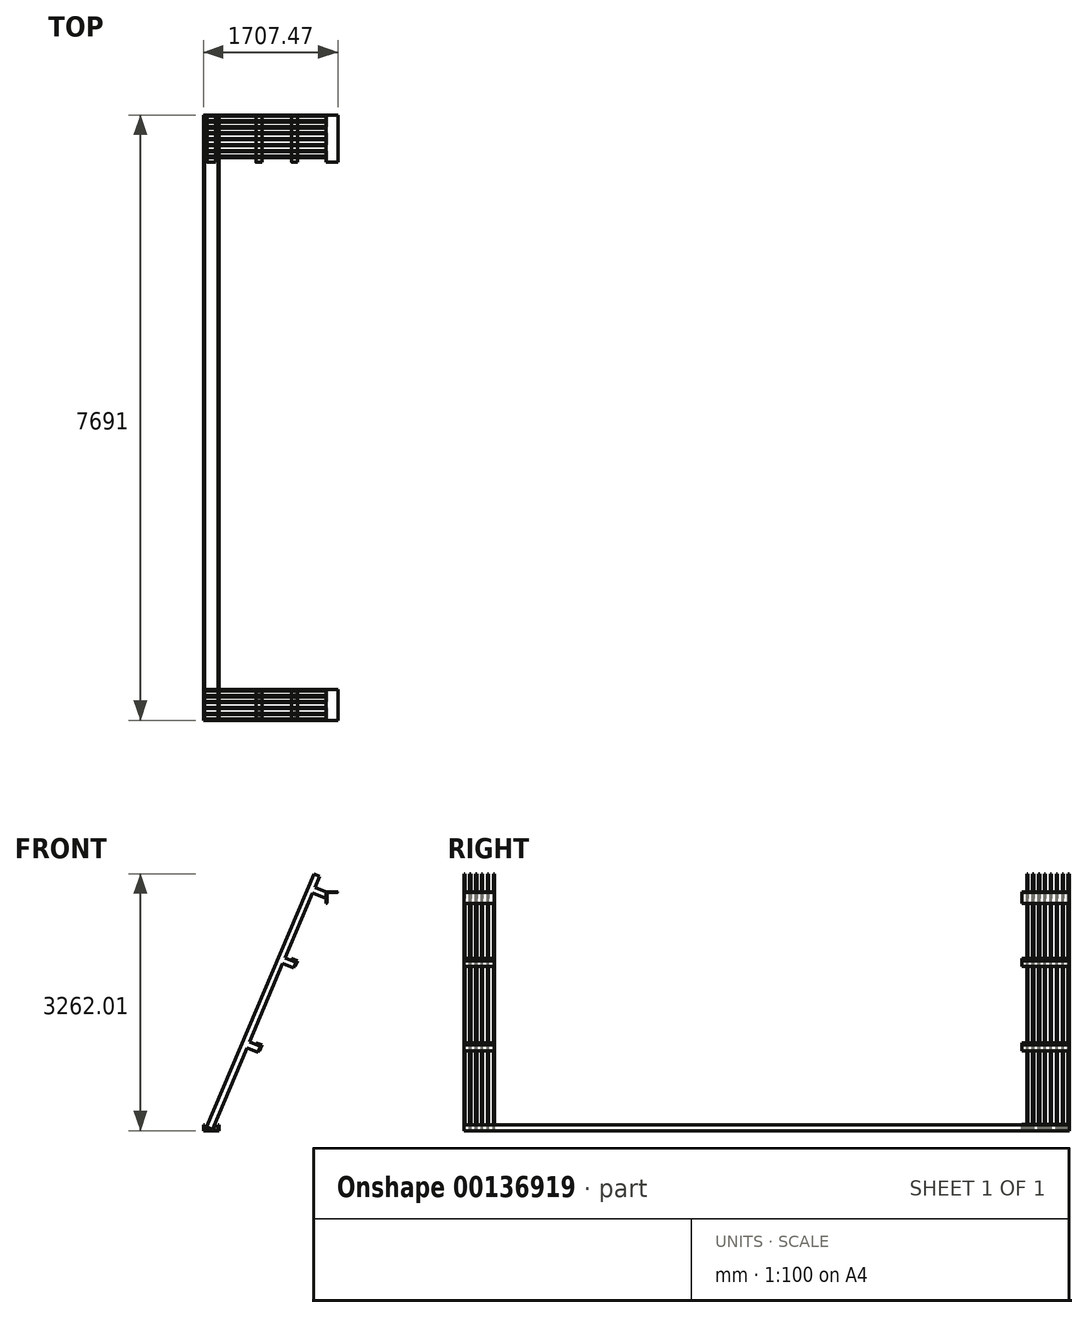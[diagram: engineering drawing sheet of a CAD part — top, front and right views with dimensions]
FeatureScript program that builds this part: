
annotation { "Feature Type Name" : "Feature", "Feature Type Description" : "" }
export const myFeature = defineFeature(function(context is Context, id is Id, definition is map)
    precondition{}
    {
        {
            var Q0;
            Q0=qCreatedBy(makeId("Front.planeOp"),FACE);
            var sketch = newSketch(context, id + "F0", { "sketchPlane" : qUnion([Q0])});
            skLineSegment(sketch, "E0", {"start": v(0, 0) * mm, "end": v(-200, 0) * mm});
            skLineSegment(sketch, "E1", {"start": v(-200, 0) * mm, "end": v(-200, 75) * mm});
            skLineSegment(sketch, "E2", {"start": v(0, 0) * mm, "end": v(0, 75) * mm});
            skLineSegment(sketch, "E3.0", {"start": v(-187.5, 18) * mm, "end": v(-187.5, 75) * mm});
            skLineSegment(sketch, "E4.0", {"start": v(-24.5, 6) * mm, "end": v(-175.5, 6) * mm});
            skLineSegment(sketch, "E5.0", {"start": v(-12.5, 18) * mm, "end": v(-12.5, 75) * mm});
            skLineSegment(sketch, "E6", {"start": v(-200, 75) * mm, "end": v(-187.5, 75) * mm});
            skLineSegment(sketch, "E7", {"start": v(-12.5, 75) * mm, "end": v(0, 75) * mm});
            skArc(sketch, "E8.filletArc", {"start": v(-187.5, 18) * mm, "mid": v(-183.99, 9.51) * mm, "end": v(-175.5, 6) * mm});
            skArc(sketch, "E9.filletArc", {"start": v(-24.5, 6) * mm, "mid": v(-16.01, 9.51) * mm, "end": v(-12.5, 18) * mm});
            skSolve(sketch);
        }
        {
            var Q0;
            Q0 = qSketchRegion(id + "F0", true);
            extrude(context, id + "F1", {"entities" : qUnion([Q0]), "depth" : 7151 * mm, "hasSecondDirection" : true, "secondDirectionOppositeDirection" : true, "secondDirectionDepth" : 540 * mm});
        }
        {
            var Q0;
            Q0=qCreatedBy(makeId("Front.planeOp"),FACE);
            var sketch = newSketch(context, id + "F2", { "sketchPlane" : qUnion([Q0])});
            skLineSegment(sketch, "E10", {"start": v(-80, 6) * mm, "end": v(-48.74, 79.64) * mm});
            skLineSegment(sketch, "E11", {"start": v(-80, 6) * mm, "end": v(-153.64, 37.26) * mm});
            skLineSegment(sketch, "E12", {"start": v(-153.64, 37.26) * mm, "end": v(-151.69, 41.86) * mm});
            skLineSegment(sketch, "E13", {"start": v(-145.13, 44.5) * mm, "end": v(-94.5, 23.02) * mm});
            skLineSegment(sketch, "E14", {"start": v(-81.4, 28.32) * mm, "end": v(-59.9, 78.95) * mm});
            skLineSegment(sketch, "E15", {"start": v(-53.34, 81.6) * mm, "end": v(-48.74, 79.64) * mm});
            skLineSegment(sketch, "E16", {"start": v(0, 0) * mm, "end": v(-293.4, 0) * mm, "construction": true});
            skPoint(sketch, "E17.visualSharp", {"position": v(-85.3, 19.11) * mm});
            skArc(sketch, "E17.filletArc", {"start": v(-94.5, 23.02) * mm, "mid": v(-86.85, 22.95) * mm, "end": v(-81.4, 28.32) * mm});
            skPoint(sketch, "E18.visualSharp", {"position": v(-57.95, 83.55) * mm});
            skArc(sketch, "E18.filletArc", {"start": v(-53.34, 81.6) * mm, "mid": v(-57.17, 81.63) * mm, "end": v(-59.9, 78.95) * mm});
            skPoint(sketch, "E19.visualSharp", {"position": v(-149.73, 46.46) * mm});
            skArc(sketch, "E19.filletArc", {"start": v(-145.13, 44.5) * mm, "mid": v(-148.96, 44.54) * mm, "end": v(-151.69, 41.86) * mm});
            skSolve(sketch);
        }
        {
            var Q0;
            Q0 = qSketchRegion(id + "F2", true);
            extrude(context, id + "F3", {"entities" : qUnion([Q0]), "oppositeDirection" : true, "depth" : 540 * mm, "hasSecondDirection" : true, "secondDirectionOppositeDirection" : false, "secondDirectionDepth" : 60 * mm});
        }
        {
            var Q0;
            Q0=qCreatedBy(makeId("Front.planeOp"),FACE);
            var sketch = newSketch(context, id + "F4", { "sketchPlane" : qUnion([Q0])});
            skLineSegment(sketch, "E20", {"start": v(541.8, 1086.98) * mm, "end": v(468.16, 1118.23) * mm});
            skLineSegment(sketch, "E21", {"start": v(541.8, 1086.98) * mm, "end": v(510.54, 1013.33) * mm});
            skLineSegment(sketch, "E22", {"start": v(510.54, 1013.33) * mm, "end": v(505.94, 1015.29) * mm});
            skLineSegment(sketch, "E23", {"start": v(503.3, 1021.84) * mm, "end": v(524.78, 1072.47) * mm});
            skLineSegment(sketch, "E24", {"start": v(519.48, 1085.58) * mm, "end": v(468.86, 1107.08) * mm});
            skLineSegment(sketch, "E25", {"start": v(466.2, 1113.63) * mm, "end": v(468.16, 1118.23) * mm});
            skLineSegment(sketch, "E26", {"start": v(210.54, 412.76) * mm, "end": v(-82.86, 412.76) * mm, "construction": true});
            skPoint(sketch, "E27.visualSharp", {"position": v(528.69, 1081.68) * mm});
            skArc(sketch, "E27.filletArc", {"start": v(524.78, 1072.47) * mm, "mid": v(524.85, 1080.13) * mm, "end": v(519.48, 1085.58) * mm});
            skPoint(sketch, "E28.visualSharp", {"position": v(464.25, 1109.03) * mm});
            skArc(sketch, "E28.filletArc", {"start": v(466.2, 1113.63) * mm, "mid": v(466.17, 1109.8) * mm, "end": v(468.86, 1107.08) * mm});
            skPoint(sketch, "E29.visualSharp", {"position": v(501.34, 1017.24) * mm});
            skArc(sketch, "E29.filletArc", {"start": v(503.3, 1021.84) * mm, "mid": v(503.26, 1018.02) * mm, "end": v(505.94, 1015.29) * mm});
            skLineSegment(sketch, "E30", {"start": v(0, 0) * mm, "end": v(-82.56, 0) * mm, "construction": true});
            skLineSegment(sketch, "E31", {"start": v(0, 0) * mm, "end": v(0, 124.95) * mm, "construction": true});
            skLineSegment(sketch, "E32", {"start": v(0, 0) * mm, "end": v(302.9, 0) * mm, "construction": true});
            skLineSegment(sketch, "E33.0", {"start": v(0, 6) * mm, "end": v(302.9, 6) * mm, "construction": true});
            skLineSegment(sketch, "E34", {"start": v(0, 6) * mm, "end": v(-80, 6) * mm, "construction": true});
            skLineSegment(sketch, "E35", {"start": v(-80, 6) * mm, "end": v(1212.93, 3051.95) * mm, "construction": true});
            skLineSegment(sketch, "E36.0", {"start": v(-89.2, 9.9) * mm, "end": v(353.5, 1052.84) * mm});
            skLineSegment(sketch, "E37", {"start": v(-80, 6) * mm, "end": v(-174.08, 45.94) * mm, "construction": true});
            skLineSegment(sketch, "E38.0", {"start": v(-76.1, 15.2) * mm, "end": v(-170.18, 55.14) * mm});
            skLineSegment(sketch, "E39.0", {"start": v(507.2, 1031.05) * mm, "end": v(284.24, 1125.69) * mm, "construction": true});
            skLineSegment(sketch, "E40.0", {"start": v(961.62, 2101.6) * mm, "end": v(738.67, 2196.24) * mm, "construction": true});
            skLineSegment(sketch, "E41.0", {"start": v(1341.8, 2997.25) * mm, "end": v(1118.85, 3091.89) * mm});
            skLineSegment(sketch, "E42.0", {"start": v(48.87, -48.7) * mm, "end": v(72.1, 6) * mm});
            skLineSegment(sketch, "E43.0", {"start": v(522.83, 1067.87) * mm, "end": v(384.75, 1126.48) * mm});
            skLineSegment(sketch, "E44.0", {"start": v(491.57, 994.23) * mm, "end": v(353.5, 1052.84) * mm});
            skLineSegment(sketch, "E45.0", {"start": v(977.25, 2138.42) * mm, "end": v(839.17, 2197.03) * mm});
            skLineSegment(sketch, "E46.0", {"start": v(945.99, 2064.78) * mm, "end": v(807.91, 2123.39) * mm});
            skLineSegment(sketch, "E47.0", {"start": v(-162.85, 41.17) * mm, "end": v(1204.32, 3262.01) * mm});
            skLineSegment(sketch, "E48.trimOffspring", {"start": v(384.75, 1126.48) * mm, "end": v(807.91, 2123.39) * mm});
            skLineSegment(sketch, "E49.trimOffspring", {"start": v(945.99, 2064.78) * mm, "end": v(977.25, 2138.42) * mm});
            skLineSegment(sketch, "E50.trimOffspring", {"start": v(491.57, 994.23) * mm, "end": v(522.83, 1067.87) * mm});
            skLineSegment(sketch, "E51.0", {"start": v(1277.96, 3230.75) * mm, "end": v(1204.32, 3262.01) * mm});
            skLineSegment(sketch, "E52.0", {"start": v(1357.43, 3034.07) * mm, "end": v(1219.35, 3092.68) * mm});
            skLineSegment(sketch, "E53.0", {"start": v(1357.43, 2947.16) * mm, "end": v(1188.1, 3019.04) * mm});
            skLineSegment(sketch, "E54.trimOffspring", {"start": v(839.17, 2197.03) * mm, "end": v(1277.96, 3230.75) * mm});
            skLineSegment(sketch, "E55", {"start": v(1357.43, 3034.07) * mm, "end": v(1357.43, 2947.16) * mm});
            skLineSegment(sketch, "E56", {"start": v(1357.43, 3034.07) * mm, "end": v(1507.43, 3034.07) * mm});
            skLineSegment(sketch, "E57", {"start": v(1357.43, 3034.07) * mm, "end": v(1357.43, 2884.07) * mm});
            skLineSegment(sketch, "E58.0", {"start": v(1383.43, 3024.07) * mm, "end": v(1499.47, 3024.07) * mm});
            skLineSegment(sketch, "E59.0", {"start": v(1367.43, 3008.07) * mm, "end": v(1367.43, 2892.07) * mm});
            skLineSegment(sketch, "E60", {"start": v(1357.43, 2884.07) * mm, "end": v(1359.43, 2884.07) * mm});
            skLineSegment(sketch, "E61", {"start": v(1507.43, 3034.07) * mm, "end": v(1507.47, 3032.25) * mm});
            skArc(sketch, "E62.filletArc", {"start": v(1383.43, 3024.07) * mm, "mid": v(1372.12, 3019.38) * mm, "end": v(1367.43, 3008.07) * mm});
            skPoint(sketch, "E63.visualSharp", {"position": v(1507.65, 3024.07) * mm});
            skArc(sketch, "E63.filletArc", {"start": v(1499.47, 3024.07) * mm, "mid": v(1505.2, 3026.47) * mm, "end": v(1507.47, 3032.25) * mm});
            skPoint(sketch, "E64.visualSharp", {"position": v(1367.43, 2884.07) * mm});
            skArc(sketch, "E64.filletArc", {"start": v(1359.43, 2884.07) * mm, "mid": v(1365.09, 2886.41) * mm, "end": v(1367.43, 2892.07) * mm});
            skLineSegment(sketch, "E65.0", {"start": v(541.8, 1086.98) * mm, "end": v(394.52, 1149.5) * mm, "construction": true});
            skLineSegment(sketch, "E66.0", {"start": v(500.77, 990.32) * mm, "end": v(541.8, 1086.98) * mm, "construction": true});
            skLineSegment(sketch, "E67", {"start": v(996.22, 2157.52) * mm, "end": v(922.58, 2188.78) * mm});
            skLineSegment(sketch, "E68", {"start": v(996.22, 2157.52) * mm, "end": v(964.96, 2083.88) * mm});
            skLineSegment(sketch, "E69", {"start": v(964.96, 2083.88) * mm, "end": v(960.36, 2085.84) * mm});
            skLineSegment(sketch, "E70", {"start": v(957.71, 2092.4) * mm, "end": v(979.2, 2143.02) * mm});
            skLineSegment(sketch, "E71", {"start": v(973.9, 2156.13) * mm, "end": v(923.28, 2177.62) * mm});
            skLineSegment(sketch, "E72", {"start": v(920.63, 2184.18) * mm, "end": v(922.58, 2188.78) * mm});
            skPoint(sketch, "E73.visualSharp", {"position": v(983.1, 2152.22) * mm});
            skArc(sketch, "E73.filletArc", {"start": v(979.2, 2143.02) * mm, "mid": v(979.27, 2150.67) * mm, "end": v(973.9, 2156.13) * mm});
            skArc(sketch, "E74.filletArc", {"start": v(920.63, 2184.18) * mm, "mid": v(920.6, 2180.35) * mm, "end": v(923.28, 2177.62) * mm});
            skPoint(sketch, "E75.visualSharp", {"position": v(955.76, 2087.79) * mm});
            skArc(sketch, "E75.filletArc", {"start": v(957.71, 2092.4) * mm, "mid": v(957.68, 2088.57) * mm, "end": v(960.36, 2085.84) * mm});
            skLineSegment(sketch, "E76.0", {"start": v(955.2, 2060.87) * mm, "end": v(996.22, 2157.52) * mm});
            skLineSegment(sketch, "E77.trimOffspring", {"start": v(858.15, 2216.13) * mm, "end": v(848.94, 2220.04) * mm});
            skSolve(sketch);
        }
        {
            var Q0;
            Q0=makeQuery(id+"F4.imprint","IMPRINT",FACE,{"disambiguationData":[TD([[makeQuery(id+"F4.imprint","IMPRINT",EDGE,{"derivedFrom":sQuery(id+"F4.wireOp",EDGE,"E20")}),1.0]])]});
            var Q1;
            {var subQ1=sQuery(id+"F4.wireOp",EDGE,"E56");Q1=makeQuery(id+"F4.imprint","IMPRINT",FACE,{"disambiguationData":[TD([[makeQuery(id+"F4.imprint","IMPRINT",EDGE,{"derivedFrom":subQ1}),-1.0]])]});}
            var Q2;
            {var subQ1=sQuery(id+"F4.wireOp",EDGE,"E69");Q2=makeQuery(id+"F4.imprint","IMPRINT",FACE,{"disambiguationData":[TD([[makeQuery(id+"F4.imprint","IMPRINT",EDGE,{"derivedFrom":subQ1}),-1.0]])]});}
            var Q3;
            {var subQ1=sQuery(id+"F4.wireOp",EDGE,"E69");Q3=makeQuery(id+"F4.imprint","IMPRINT",FACE,{"disambiguationData":[TD([[makeQuery(id+"F4.imprint","IMPRINT",EDGE,{"derivedFrom":subQ1}),-1.0]])]});}
            extrude(context, id + "F5", {"entities" : qUnion([Q0, Q1, Q2, Q3]), "oppositeDirection" : true, "depth" : 540 * mm, "hasSecondDirection" : true, "secondDirectionOppositeDirection" : false, "secondDirectionDepth" : 60 * mm});
        }
        {
            var Q0;
            {var subQ4=sQuery(id+"F4.wireOp",EDGE,"E51.0");Q0=makeQuery(id+"F4.imprint","IMPRINT",FACE,{"disambiguationData":[TD([[makeQuery(id+"F4.imprint","IMPRINT",EDGE,{"derivedFrom":subQ4}),1.0]])]});}
            var Q1;
            {var subQ10=sQuery(id+"F4.wireOp",EDGE,"E43.0");Q1=makeQuery(id+"F4.imprint","IMPRINT",FACE,{"disambiguationData":[TD([[makeQuery(id+"F4.imprint","IMPRINT",EDGE,{"derivedFrom":subQ10}),1.0]])]});}
            var Q2;
            {var subQ1=sQuery(id+"F4.wireOp",EDGE,"E52.0");Q2=makeQuery(id+"F4.imprint","IMPRINT",FACE,{"disambiguationData":[TD([[makeQuery(id+"F4.imprint","IMPRINT",EDGE,{"derivedFrom":subQ1}),1.0]])]});}
            extrude(context, id + "F6", {"entities" : qUnion([Q0, Q1, Q2]), "oppositeDirection" : true, "depth" : 15 * mm});
        }
        {
            var Q0;
            Q0=qCreatedBy(makeId("Front.planeOp"),FACE);
            cPlane(context, id + "F7", {"entities" : qUnion([Q0]), "cplaneType" : CPlaneType.OFFSET, "offset" : 90 * mm, "oppositeDirection" : true, "width" : 150 * mm, "height" : 150 * mm});
        }
        {
            var Q0;
            Q0=qCreatedBy(id+"F7.planeOp",FACE);
            var sketch = newSketch(context, id + "F8", { "sketchPlane" : qUnion([Q0])});
            skLineSegment(sketch, "E78", {"start": v(541.8, 1086.98) * mm, "end": v(468.16, 1118.23) * mm});
            skLineSegment(sketch, "E79", {"start": v(541.8, 1086.98) * mm, "end": v(510.54, 1013.33) * mm});
            skLineSegment(sketch, "E80", {"start": v(510.54, 1013.33) * mm, "end": v(505.94, 1015.29) * mm});
            skLineSegment(sketch, "E81", {"start": v(503.3, 1021.84) * mm, "end": v(524.78, 1072.47) * mm});
            skLineSegment(sketch, "E82", {"start": v(519.48, 1085.58) * mm, "end": v(468.86, 1107.08) * mm});
            skLineSegment(sketch, "E83", {"start": v(466.2, 1113.63) * mm, "end": v(468.16, 1118.23) * mm});
            skLineSegment(sketch, "E84", {"start": v(1436.56, -795.55) * mm, "end": v(1143.16, -795.55) * mm, "construction": true});
            skPoint(sketch, "E85.visualSharp", {"position": v(528.69, 1081.68) * mm});
            skArc(sketch, "E85.filletArc", {"start": v(524.78, 1072.47) * mm, "mid": v(524.85, 1080.13) * mm, "end": v(519.48, 1085.58) * mm});
            skPoint(sketch, "E86.visualSharp", {"position": v(464.25, 1109.03) * mm});
            skArc(sketch, "E86.filletArc", {"start": v(466.2, 1113.63) * mm, "mid": v(466.17, 1109.8) * mm, "end": v(468.86, 1107.08) * mm});
            skPoint(sketch, "E87.visualSharp", {"position": v(501.34, 1017.24) * mm});
            skArc(sketch, "E87.filletArc", {"start": v(503.3, 1021.84) * mm, "mid": v(503.26, 1018.02) * mm, "end": v(505.94, 1015.29) * mm});
            skLineSegment(sketch, "E88", {"start": v(0, 0) * mm, "end": v(-82.56, 0) * mm, "construction": true});
            skLineSegment(sketch, "E89", {"start": v(0, 0) * mm, "end": v(0, 124.95) * mm, "construction": true});
            skLineSegment(sketch, "E90", {"start": v(0, 0) * mm, "end": v(302.9, 0) * mm, "construction": true});
            skLineSegment(sketch, "E91.0", {"start": v(0, 6) * mm, "end": v(302.9, 6) * mm, "construction": true});
            skLineSegment(sketch, "E92", {"start": v(0, 6) * mm, "end": v(-80, 6) * mm, "construction": true});
            skLineSegment(sketch, "E93", {"start": v(-80, 6) * mm, "end": v(1212.93, 3051.95) * mm, "construction": true});
            skLineSegment(sketch, "E94.0", {"start": v(-89.2, 9.9) * mm, "end": v(353.5, 1052.84) * mm});
            skLineSegment(sketch, "E95", {"start": v(-80, 6) * mm, "end": v(-174.08, 45.94) * mm, "construction": true});
            skLineSegment(sketch, "E96.0", {"start": v(-76.1, 15.2) * mm, "end": v(-170.18, 55.14) * mm});
            skLineSegment(sketch, "E97.0", {"start": v(507.2, 1031.05) * mm, "end": v(284.24, 1125.69) * mm, "construction": true});
            skLineSegment(sketch, "E98.0", {"start": v(961.62, 2101.6) * mm, "end": v(738.67, 2196.24) * mm, "construction": true});
            skLineSegment(sketch, "E99.0", {"start": v(1341.8, 2997.25) * mm, "end": v(1118.85, 3091.89) * mm});
            skLineSegment(sketch, "E100.0", {"start": v(48.87, -48.7) * mm, "end": v(72.1, 6) * mm});
            skLineSegment(sketch, "E101.0", {"start": v(522.83, 1067.87) * mm, "end": v(384.75, 1126.48) * mm});
            skLineSegment(sketch, "E102.0", {"start": v(491.57, 994.23) * mm, "end": v(353.5, 1052.84) * mm});
            skLineSegment(sketch, "E103.0", {"start": v(977.25, 2138.42) * mm, "end": v(839.17, 2197.03) * mm});
            skLineSegment(sketch, "E104.0", {"start": v(945.99, 2064.78) * mm, "end": v(807.91, 2123.39) * mm});
            skLineSegment(sketch, "E105.0", {"start": v(-162.85, 41.17) * mm, "end": v(1204.32, 3262.01) * mm});
            skLineSegment(sketch, "E106.trimOffspring", {"start": v(384.75, 1126.48) * mm, "end": v(807.91, 2123.39) * mm});
            skLineSegment(sketch, "E107.trimOffspring", {"start": v(945.99, 2064.78) * mm, "end": v(977.25, 2138.42) * mm});
            skLineSegment(sketch, "E108.trimOffspring", {"start": v(491.57, 994.23) * mm, "end": v(522.83, 1067.87) * mm});
            skLineSegment(sketch, "E109.0", {"start": v(1277.96, 3230.75) * mm, "end": v(1204.32, 3262.01) * mm});
            skLineSegment(sketch, "E110.0", {"start": v(1357.43, 3034.07) * mm, "end": v(1219.35, 3092.68) * mm});
            skLineSegment(sketch, "E111.0", {"start": v(1357.43, 2947.16) * mm, "end": v(1188.1, 3019.04) * mm});
            skLineSegment(sketch, "E112.trimOffspring", {"start": v(839.17, 2197.03) * mm, "end": v(1277.96, 3230.75) * mm});
            skLineSegment(sketch, "E113", {"start": v(1357.43, 3034.07) * mm, "end": v(1357.43, 2947.16) * mm});
            skLineSegment(sketch, "E114", {"start": v(1357.43, 3034.07) * mm, "end": v(1507.43, 3034.07) * mm});
            skLineSegment(sketch, "E115", {"start": v(1357.43, 3034.07) * mm, "end": v(1357.43, 2884.07) * mm});
            skLineSegment(sketch, "E116.0", {"start": v(1383.43, 3024.07) * mm, "end": v(1499.47, 3024.07) * mm});
            skLineSegment(sketch, "E117.0", {"start": v(1367.43, 3008.07) * mm, "end": v(1367.43, 2892.07) * mm});
            skLineSegment(sketch, "E118", {"start": v(1357.43, 2884.07) * mm, "end": v(1359.43, 2884.07) * mm});
            skLineSegment(sketch, "E119", {"start": v(1507.43, 3034.07) * mm, "end": v(1507.47, 3032.25) * mm});
            skArc(sketch, "E120.filletArc", {"start": v(1383.43, 3024.07) * mm, "mid": v(1372.12, 3019.38) * mm, "end": v(1367.43, 3008.07) * mm});
            skPoint(sketch, "E121.visualSharp", {"position": v(1507.65, 3024.07) * mm});
            skArc(sketch, "E121.filletArc", {"start": v(1499.47, 3024.07) * mm, "mid": v(1505.2, 3026.47) * mm, "end": v(1507.47, 3032.25) * mm});
            skPoint(sketch, "E122.visualSharp", {"position": v(1367.43, 2884.07) * mm});
            skArc(sketch, "E122.filletArc", {"start": v(1359.43, 2884.07) * mm, "mid": v(1365.09, 2886.41) * mm, "end": v(1367.43, 2892.07) * mm});
            skLineSegment(sketch, "E123.0", {"start": v(541.8, 1086.98) * mm, "end": v(394.52, 1149.5) * mm, "construction": true});
            skLineSegment(sketch, "E124.0", {"start": v(500.77, 990.32) * mm, "end": v(541.8, 1086.98) * mm, "construction": true});
            skLineSegment(sketch, "E125", {"start": v(996.22, 2157.52) * mm, "end": v(922.58, 2188.78) * mm});
            skLineSegment(sketch, "E126", {"start": v(996.22, 2157.52) * mm, "end": v(964.96, 2083.88) * mm});
            skLineSegment(sketch, "E127", {"start": v(964.96, 2083.88) * mm, "end": v(960.36, 2085.84) * mm});
            skLineSegment(sketch, "E128", {"start": v(957.71, 2092.4) * mm, "end": v(979.2, 2143.02) * mm});
            skLineSegment(sketch, "E129", {"start": v(973.9, 2156.13) * mm, "end": v(923.28, 2177.62) * mm});
            skLineSegment(sketch, "E130", {"start": v(920.63, 2184.18) * mm, "end": v(922.58, 2188.78) * mm});
            skPoint(sketch, "E131.visualSharp", {"position": v(983.1, 2152.22) * mm});
            skArc(sketch, "E131.filletArc", {"start": v(979.2, 2143.02) * mm, "mid": v(979.27, 2150.67) * mm, "end": v(973.9, 2156.13) * mm});
            skArc(sketch, "E132.filletArc", {"start": v(920.63, 2184.18) * mm, "mid": v(920.6, 2180.35) * mm, "end": v(923.28, 2177.62) * mm});
            skPoint(sketch, "E133.visualSharp", {"position": v(955.76, 2087.79) * mm});
            skArc(sketch, "E133.filletArc", {"start": v(957.71, 2092.4) * mm, "mid": v(957.68, 2088.57) * mm, "end": v(960.36, 2085.84) * mm});
            skLineSegment(sketch, "E134.0", {"start": v(955.2, 2060.87) * mm, "end": v(996.22, 2157.52) * mm});
            skLineSegment(sketch, "E135.trimOffspring", {"start": v(858.15, 2216.13) * mm, "end": v(848.94, 2220.04) * mm});
            skLineSegment(sketch, "E136", {"start": v(1219.35, 3092.68) * mm, "end": v(1250.61, 3166.32) * mm});
            skLineSegment(sketch, "E137", {"start": v(1250.61, 3166.32) * mm, "end": v(1324.25, 3135.06) * mm});
            skLineSegment(sketch, "E138", {"start": v(1324.25, 3135.06) * mm, "end": v(1293, 3061.42) * mm});
            skLineSegment(sketch, "E139", {"start": v(1293, 3061.42) * mm, "end": v(1219.35, 3092.68) * mm});
            skCircle(sketch, "E140", {"center": v(1271.8, 3113.87) * mm, "radius": 12.89 * mm});
            skSolve(sketch);
        }
        {
            var Q0;
            {var subQ16=sQuery(id+"F8.wireOp",EDGE,"E101.0");Q0=makeQuery(id+"F8.imprint","IMPRINT",FACE,{"disambiguationData":[TD([[makeQuery(id+"F8.imprint","IMPRINT",EDGE,{"derivedFrom":subQ16}),1.0]])]});}
            var Q1;
            {var subQ4=sQuery(id+"F8.wireOp",EDGE,"E110.0");Q1=makeQuery(id+"F8.imprint","IMPRINT",FACE,{"disambiguationData":[TD([[makeQuery(id+"F8.imprint","IMPRINT",EDGE,{"derivedFrom":subQ4}),1.0]])]});}
            var Q2;
            Q2=makeQuery(id+"F8.imprint","IMPRINT",FACE,{"disambiguationData":[TD([[makeQuery(id+"F8.imprint","IMPRINT",EDGE,{"derivedFrom":sQuery(id+"F8.wireOp",EDGE,"E136")}),-1.0]])]});
            var Q3;
            {var subQ4=sQuery(id+"F8.wireOp",EDGE,"E109.0");Q3=makeQuery(id+"F8.imprint","IMPRINT",FACE,{"disambiguationData":[TD([[makeQuery(id+"F8.imprint","IMPRINT",EDGE,{"derivedFrom":subQ4}),1.0]])]});}
            extrude(context, id + "F9", {"entities" : qUnion([Q0, Q1, Q2, Q3]), "depth" : 15 * mm});
        }
        {
            var Q0;
            Q0=makeQuery(id+"F6.opExtrude","SWEPT_BODY",BODY,{"disambiguationData":[OSD([sQuery(id+"F4.wireOp",EDGE,"E36.0"),sQuery(id+"F4.wireOp",EDGE,"E38.0"),sQuery(id+"F4.wireOp",EDGE,"E43.0"),sQuery(id+"F4.wireOp",EDGE,"E44.0"),sQuery(id+"F4.wireOp",EDGE,"E45.0"),sQuery(id+"F4.wireOp",EDGE,"E46.0"),sQuery(id+"F4.wireOp",EDGE,"E47.0"),sQuery(id+"F4.wireOp",EDGE,"E48.trimOffspring"),sQuery(id+"F4.wireOp",EDGE,"E49.trimOffspring"),sQuery(id+"F4.wireOp",EDGE,"E50.trimOffspring"),sQuery(id+"F4.wireOp",EDGE,"E51.0"),sQuery(id+"F4.wireOp",EDGE,"E52.0"),sQuery(id+"F4.wireOp",EDGE,"E53.0"),sQuery(id+"F4.wireOp",EDGE,"E54.trimOffspring"),sQuery(id+"F4.wireOp",EDGE,"E57"),sQuery(id+"F4.wireOp",EDGE,"E70")])]});
            var Q1;
            Q1=makeQuery(id+"F5.opExtrude","SWEPT_EDGE",EDGE,{"disambiguationData":[OSD([sQuery(id+"F4.wireOp",EDGE,"E52.0"),sQuery(id+"F4.wireOp",EDGE,"E56"),sQuery(id+"F4.wireOp",EDGE,"E57")])]});
            transform(context, id + "F10", {"entities" : qUnion([Q0]), "transformType" : TransformType.TRANSLATION_3D, "dx" : 0 * mm, "dy" : 150 * mm, "dz" : 0 * mm, "makeCopy" : true});
        }
        {
            var Q0;
            Q0=makeQuery(id+"F10.opPattern","COPY",BODY,{"derivedFrom":makeQuery(id+"F6.opExtrude","SWEPT_BODY",BODY,{"disambiguationData":[OSD([sQuery(id+"F4.wireOp",EDGE,"E36.0"),sQuery(id+"F4.wireOp",EDGE,"E38.0"),sQuery(id+"F4.wireOp",EDGE,"E43.0"),sQuery(id+"F4.wireOp",EDGE,"E44.0"),sQuery(id+"F4.wireOp",EDGE,"E45.0"),sQuery(id+"F4.wireOp",EDGE,"E46.0"),sQuery(id+"F4.wireOp",EDGE,"E47.0"),sQuery(id+"F4.wireOp",EDGE,"E48.trimOffspring"),sQuery(id+"F4.wireOp",EDGE,"E49.trimOffspring"),sQuery(id+"F4.wireOp",EDGE,"E50.trimOffspring"),sQuery(id+"F4.wireOp",EDGE,"E51.0"),sQuery(id+"F4.wireOp",EDGE,"E52.0"),sQuery(id+"F4.wireOp",EDGE,"E53.0"),sQuery(id+"F4.wireOp",EDGE,"E54.trimOffspring"),sQuery(id+"F4.wireOp",EDGE,"E57"),sQuery(id+"F4.wireOp",EDGE,"E70")])]}),"instanceName":"1"});
            transform(context, id + "F11", {"entities" : qUnion([Q0]), "transformType" : TransformType.TRANSLATION_3D, "dx" : 0 * mm, "dy" : 75 * mm, "dz" : 0 * mm, "makeCopy" : true});
        }
        {
            var Q0;
            Q0=makeQuery(id+"F11.opPattern","COPY",BODY,{"derivedFrom":makeQuery(id+"F10.opPattern","COPY",BODY,{"derivedFrom":makeQuery(id+"F6.opExtrude","SWEPT_BODY",BODY,{"disambiguationData":[OSD([sQuery(id+"F4.wireOp",EDGE,"E36.0"),sQuery(id+"F4.wireOp",EDGE,"E38.0"),sQuery(id+"F4.wireOp",EDGE,"E43.0"),sQuery(id+"F4.wireOp",EDGE,"E44.0"),sQuery(id+"F4.wireOp",EDGE,"E45.0"),sQuery(id+"F4.wireOp",EDGE,"E46.0"),sQuery(id+"F4.wireOp",EDGE,"E47.0"),sQuery(id+"F4.wireOp",EDGE,"E48.trimOffspring"),sQuery(id+"F4.wireOp",EDGE,"E49.trimOffspring"),sQuery(id+"F4.wireOp",EDGE,"E50.trimOffspring"),sQuery(id+"F4.wireOp",EDGE,"E51.0"),sQuery(id+"F4.wireOp",EDGE,"E52.0"),sQuery(id+"F4.wireOp",EDGE,"E53.0"),sQuery(id+"F4.wireOp",EDGE,"E54.trimOffspring"),sQuery(id+"F4.wireOp",EDGE,"E57"),sQuery(id+"F4.wireOp",EDGE,"E70")])]}),"instanceName":"1"}),"instanceName":"1"});
            transform(context, id + "F12", {"entities" : qUnion([Q0]), "transformType" : TransformType.TRANSLATION_3D, "dx" : 0 * mm, "dy" : 75 * mm, "dz" : 0 * mm, "makeCopy" : true});
        }
        {
            var Q0;
            Q0=makeQuery(id+"F12.opPattern","COPY",BODY,{"derivedFrom":makeQuery(id+"F11.opPattern","COPY",BODY,{"derivedFrom":makeQuery(id+"F10.opPattern","COPY",BODY,{"derivedFrom":makeQuery(id+"F6.opExtrude","SWEPT_BODY",BODY,{"disambiguationData":[OSD([sQuery(id+"F4.wireOp",EDGE,"E36.0"),sQuery(id+"F4.wireOp",EDGE,"E38.0"),sQuery(id+"F4.wireOp",EDGE,"E43.0"),sQuery(id+"F4.wireOp",EDGE,"E44.0"),sQuery(id+"F4.wireOp",EDGE,"E45.0"),sQuery(id+"F4.wireOp",EDGE,"E46.0"),sQuery(id+"F4.wireOp",EDGE,"E47.0"),sQuery(id+"F4.wireOp",EDGE,"E48.trimOffspring"),sQuery(id+"F4.wireOp",EDGE,"E49.trimOffspring"),sQuery(id+"F4.wireOp",EDGE,"E50.trimOffspring"),sQuery(id+"F4.wireOp",EDGE,"E51.0"),sQuery(id+"F4.wireOp",EDGE,"E52.0"),sQuery(id+"F4.wireOp",EDGE,"E53.0"),sQuery(id+"F4.wireOp",EDGE,"E54.trimOffspring"),sQuery(id+"F4.wireOp",EDGE,"E57"),sQuery(id+"F4.wireOp",EDGE,"E70")])]}),"instanceName":"1"}),"instanceName":"1"}),"instanceName":"1"});
            transform(context, id + "F13", {"entities" : qUnion([Q0]), "transformType" : TransformType.TRANSLATION_3D, "dx" : 0 * mm, "dy" : 75 * mm, "dz" : 0 * mm, "makeCopy" : true});
        }
        {
            var Q0;
            Q0=makeQuery(id+"F9.opExtrude","SWEPT_BODY",BODY,{"disambiguationData":[OSD([sQuery(id+"F8.wireOp",EDGE,"E94.0"),sQuery(id+"F8.wireOp",EDGE,"E96.0"),sQuery(id+"F8.wireOp",EDGE,"E101.0"),sQuery(id+"F8.wireOp",EDGE,"E102.0"),sQuery(id+"F8.wireOp",EDGE,"E103.0"),sQuery(id+"F8.wireOp",EDGE,"E104.0"),sQuery(id+"F8.wireOp",EDGE,"E105.0"),sQuery(id+"F8.wireOp",EDGE,"E106.trimOffspring"),sQuery(id+"F8.wireOp",EDGE,"E107.trimOffspring"),sQuery(id+"F8.wireOp",EDGE,"E108.trimOffspring"),sQuery(id+"F8.wireOp",EDGE,"E109.0"),sQuery(id+"F8.wireOp",EDGE,"E110.0"),sQuery(id+"F8.wireOp",EDGE,"E111.0"),sQuery(id+"F8.wireOp",EDGE,"E112.trimOffspring"),sQuery(id+"F8.wireOp",EDGE,"E115"),sQuery(id+"F8.wireOp",EDGE,"E128"),sQuery(id+"F8.wireOp",EDGE,"E137"),sQuery(id+"F8.wireOp",EDGE,"E138"),sQuery(id+"F8.wireOp",EDGE,"E140")])]});
            transform(context, id + "F14", {"entities" : qUnion([Q0]), "transformType" : TransformType.TRANSLATION_3D, "dx" : 0 * mm, "dy" : 375 * mm, "dz" : 0 * mm, "makeCopy" : true});
        }
        {
            var Q0;
            Q0=makeQuery(id+"F13.opPattern","COPY",BODY,{"derivedFrom":makeQuery(id+"F12.opPattern","COPY",BODY,{"derivedFrom":makeQuery(id+"F11.opPattern","COPY",BODY,{"derivedFrom":makeQuery(id+"F10.opPattern","COPY",BODY,{"derivedFrom":makeQuery(id+"F6.opExtrude","SWEPT_BODY",BODY,{"disambiguationData":[OSD([sQuery(id+"F4.wireOp",EDGE,"E36.0"),sQuery(id+"F4.wireOp",EDGE,"E38.0"),sQuery(id+"F4.wireOp",EDGE,"E43.0"),sQuery(id+"F4.wireOp",EDGE,"E44.0"),sQuery(id+"F4.wireOp",EDGE,"E45.0"),sQuery(id+"F4.wireOp",EDGE,"E46.0"),sQuery(id+"F4.wireOp",EDGE,"E47.0"),sQuery(id+"F4.wireOp",EDGE,"E48.trimOffspring"),sQuery(id+"F4.wireOp",EDGE,"E49.trimOffspring"),sQuery(id+"F4.wireOp",EDGE,"E50.trimOffspring"),sQuery(id+"F4.wireOp",EDGE,"E51.0"),sQuery(id+"F4.wireOp",EDGE,"E52.0"),sQuery(id+"F4.wireOp",EDGE,"E53.0"),sQuery(id+"F4.wireOp",EDGE,"E54.trimOffspring"),sQuery(id+"F4.wireOp",EDGE,"E57"),sQuery(id+"F4.wireOp",EDGE,"E70")])]}),"instanceName":"1"}),"instanceName":"1"}),"instanceName":"1"}),"instanceName":"1"});
            transform(context, id + "F15", {"entities" : qUnion([Q0]), "transformType" : TransformType.TRANSLATION_3D, "dx" : 0 * mm, "dy" : 150 * mm, "dz" : 0 * mm, "makeCopy" : true});
        }
        {
            var Q0;
            Q0=makeQuery(id+"F1.opExtrude","CAP_FACE",FACE,{"disambiguationData":[OSD([sQuery(id+"F0.wireOp",EDGE,"E0"),sQuery(id+"F0.wireOp",EDGE,"E1"),sQuery(id+"F0.wireOp",EDGE,"E2"),sQuery(id+"F0.wireOp",EDGE,"E3.0"),sQuery(id+"F0.wireOp",EDGE,"E4.0"),sQuery(id+"F0.wireOp",EDGE,"E5.0"),sQuery(id+"F0.wireOp",EDGE,"E6"),sQuery(id+"F0.wireOp",EDGE,"E7"),sQuery(id+"F0.wireOp",EDGE,"E8.filletArc"),sQuery(id+"F0.wireOp",EDGE,"E9.filletArc")])],"isStart":false});
            var sketch = newSketch(context, id + "F16", { "sketchPlane" : qUnion([Q0])});
            skLineSegment(sketch, "E141", {"start": v(541.8, 1086.98) * mm, "end": v(468.16, 1118.23) * mm});
            skLineSegment(sketch, "E142", {"start": v(541.8, 1086.98) * mm, "end": v(510.54, 1013.33) * mm});
            skLineSegment(sketch, "E143", {"start": v(510.54, 1013.33) * mm, "end": v(505.94, 1015.29) * mm});
            skLineSegment(sketch, "E144", {"start": v(503.3, 1021.84) * mm, "end": v(524.78, 1072.47) * mm});
            skLineSegment(sketch, "E145", {"start": v(519.48, 1085.58) * mm, "end": v(468.86, 1107.08) * mm});
            skLineSegment(sketch, "E146", {"start": v(466.2, 1113.63) * mm, "end": v(468.16, 1118.23) * mm});
            skLineSegment(sketch, "E147", {"start": v(863.72, 67.88) * mm, "end": v(570.32, 67.88) * mm, "construction": true});
            skPoint(sketch, "E148.visualSharp", {"position": v(528.69, 1081.68) * mm});
            skArc(sketch, "E148.filletArc", {"start": v(524.78, 1072.47) * mm, "mid": v(524.85, 1080.13) * mm, "end": v(519.48, 1085.58) * mm});
            skPoint(sketch, "E149.visualSharp", {"position": v(464.25, 1109.03) * mm});
            skArc(sketch, "E149.filletArc", {"start": v(466.2, 1113.63) * mm, "mid": v(466.17, 1109.8) * mm, "end": v(468.86, 1107.08) * mm});
            skPoint(sketch, "E150.visualSharp", {"position": v(501.34, 1017.24) * mm});
            skArc(sketch, "E150.filletArc", {"start": v(503.3, 1021.84) * mm, "mid": v(503.26, 1018.02) * mm, "end": v(505.94, 1015.29) * mm});
            skLineSegment(sketch, "E151", {"start": v(0, 0) * mm, "end": v(-82.56, 0) * mm, "construction": true});
            skLineSegment(sketch, "E152", {"start": v(0, 0) * mm, "end": v(0, 124.95) * mm, "construction": true});
            skLineSegment(sketch, "E153", {"start": v(0, 0) * mm, "end": v(302.9, 0) * mm, "construction": true});
            skLineSegment(sketch, "E154.0", {"start": v(0, 6) * mm, "end": v(302.9, 6) * mm, "construction": true});
            skLineSegment(sketch, "E155", {"start": v(0, 6) * mm, "end": v(-80, 6) * mm, "construction": true});
            skLineSegment(sketch, "E156", {"start": v(-80, 6) * mm, "end": v(1212.93, 3051.95) * mm, "construction": true});
            skLineSegment(sketch, "E157.0", {"start": v(-89.2, 9.9) * mm, "end": v(353.5, 1052.84) * mm});
            skLineSegment(sketch, "E158", {"start": v(-80, 6) * mm, "end": v(-174.08, 45.94) * mm, "construction": true});
            skLineSegment(sketch, "E159.0", {"start": v(-76.1, 15.2) * mm, "end": v(-170.18, 55.14) * mm});
            skLineSegment(sketch, "E160.0", {"start": v(507.2, 1031.05) * mm, "end": v(284.24, 1125.69) * mm, "construction": true});
            skLineSegment(sketch, "E161.0", {"start": v(961.62, 2101.6) * mm, "end": v(738.67, 2196.24) * mm, "construction": true});
            skLineSegment(sketch, "E162.0", {"start": v(1341.8, 2997.25) * mm, "end": v(1118.85, 3091.89) * mm});
            skLineSegment(sketch, "E163.0", {"start": v(48.87, -48.7) * mm, "end": v(72.1, 6) * mm});
            skLineSegment(sketch, "E164.0", {"start": v(522.83, 1067.87) * mm, "end": v(384.75, 1126.48) * mm});
            skLineSegment(sketch, "E165.0", {"start": v(491.57, 994.23) * mm, "end": v(353.5, 1052.84) * mm});
            skLineSegment(sketch, "E166.0", {"start": v(977.25, 2138.42) * mm, "end": v(839.17, 2197.03) * mm});
            skLineSegment(sketch, "E167.0", {"start": v(945.99, 2064.78) * mm, "end": v(807.91, 2123.39) * mm});
            skLineSegment(sketch, "E168.0", {"start": v(-162.85, 41.17) * mm, "end": v(1204.32, 3262.01) * mm});
            skLineSegment(sketch, "E169.trimOffspring", {"start": v(384.75, 1126.48) * mm, "end": v(807.91, 2123.39) * mm});
            skLineSegment(sketch, "E170.trimOffspring", {"start": v(945.99, 2064.78) * mm, "end": v(977.25, 2138.42) * mm});
            skLineSegment(sketch, "E171.trimOffspring", {"start": v(491.57, 994.23) * mm, "end": v(522.83, 1067.87) * mm});
            skLineSegment(sketch, "E172.0", {"start": v(1277.96, 3230.75) * mm, "end": v(1204.32, 3262.01) * mm});
            skLineSegment(sketch, "E173.0", {"start": v(1357.43, 3034.07) * mm, "end": v(1219.35, 3092.68) * mm});
            skLineSegment(sketch, "E174.0", {"start": v(1357.43, 2947.16) * mm, "end": v(1188.1, 3019.04) * mm});
            skLineSegment(sketch, "E175.trimOffspring", {"start": v(839.17, 2197.03) * mm, "end": v(1277.96, 3230.75) * mm});
            skLineSegment(sketch, "E176", {"start": v(1357.43, 3034.07) * mm, "end": v(1357.43, 2947.16) * mm});
            skLineSegment(sketch, "E177", {"start": v(1357.43, 3034.07) * mm, "end": v(1507.43, 3034.07) * mm});
            skLineSegment(sketch, "E178", {"start": v(1357.43, 3034.07) * mm, "end": v(1357.43, 2884.07) * mm});
            skLineSegment(sketch, "E179.0", {"start": v(1383.43, 3024.07) * mm, "end": v(1499.47, 3024.07) * mm});
            skLineSegment(sketch, "E180.0", {"start": v(1367.43, 3008.07) * mm, "end": v(1367.43, 2892.07) * mm});
            skLineSegment(sketch, "E181", {"start": v(1357.43, 2884.07) * mm, "end": v(1359.43, 2884.07) * mm});
            skLineSegment(sketch, "E182", {"start": v(1507.43, 3034.07) * mm, "end": v(1507.47, 3032.25) * mm});
            skArc(sketch, "E183.filletArc", {"start": v(1383.43, 3024.07) * mm, "mid": v(1372.12, 3019.38) * mm, "end": v(1367.43, 3008.07) * mm});
            skPoint(sketch, "E184.visualSharp", {"position": v(1507.65, 3024.07) * mm});
            skArc(sketch, "E184.filletArc", {"start": v(1499.47, 3024.07) * mm, "mid": v(1505.2, 3026.47) * mm, "end": v(1507.47, 3032.25) * mm});
            skPoint(sketch, "E185.visualSharp", {"position": v(1367.43, 2884.07) * mm});
            skArc(sketch, "E185.filletArc", {"start": v(1359.43, 2884.07) * mm, "mid": v(1365.09, 2886.41) * mm, "end": v(1367.43, 2892.07) * mm});
            skLineSegment(sketch, "E186.0", {"start": v(541.8, 1086.98) * mm, "end": v(394.52, 1149.5) * mm, "construction": true});
            skLineSegment(sketch, "E187.0", {"start": v(500.77, 990.32) * mm, "end": v(541.8, 1086.98) * mm, "construction": true});
            skLineSegment(sketch, "E188", {"start": v(996.22, 2157.52) * mm, "end": v(922.58, 2188.78) * mm});
            skLineSegment(sketch, "E189", {"start": v(996.22, 2157.52) * mm, "end": v(964.96, 2083.88) * mm});
            skLineSegment(sketch, "E190", {"start": v(964.96, 2083.88) * mm, "end": v(960.36, 2085.84) * mm});
            skLineSegment(sketch, "E191", {"start": v(957.71, 2092.4) * mm, "end": v(979.2, 2143.02) * mm});
            skLineSegment(sketch, "E192", {"start": v(973.9, 2156.13) * mm, "end": v(923.28, 2177.62) * mm});
            skLineSegment(sketch, "E193", {"start": v(920.63, 2184.18) * mm, "end": v(922.58, 2188.78) * mm});
            skPoint(sketch, "E194.visualSharp", {"position": v(983.1, 2152.22) * mm});
            skArc(sketch, "E194.filletArc", {"start": v(979.2, 2143.02) * mm, "mid": v(979.27, 2150.67) * mm, "end": v(973.9, 2156.13) * mm});
            skArc(sketch, "E195.filletArc", {"start": v(920.63, 2184.18) * mm, "mid": v(920.6, 2180.35) * mm, "end": v(923.28, 2177.62) * mm});
            skPoint(sketch, "E196.visualSharp", {"position": v(955.76, 2087.79) * mm});
            skArc(sketch, "E196.filletArc", {"start": v(957.71, 2092.4) * mm, "mid": v(957.68, 2088.57) * mm, "end": v(960.36, 2085.84) * mm});
            skLineSegment(sketch, "E197.0", {"start": v(955.2, 2060.87) * mm, "end": v(996.22, 2157.52) * mm});
            skLineSegment(sketch, "E198.trimOffspring", {"start": v(858.15, 2216.13) * mm, "end": v(848.94, 2220.04) * mm});
            skSolve(sketch);
        }
        {
            var Q0;
            {var subQ7=sQuery(id+"F16.wireOp",EDGE,"E164.0");Q0=makeQuery(id+"F16.imprint","IMPRINT",FACE,{"disambiguationData":[TD([[makeQuery(id+"F16.imprint","IMPRINT",EDGE,{"derivedFrom":subQ7}),1.0]])]});}
            var Q1;
            {var subQ0=sQuery(id+"F16.wireOp",EDGE,"E172.0");Q1=makeQuery(id+"F16.imprint","IMPRINT",FACE,{"disambiguationData":[TD([[makeQuery(id+"F16.imprint","IMPRINT",EDGE,{"derivedFrom":subQ0}),1.0]])]});}
            var Q2;
            {var subQ1=sQuery(id+"F16.wireOp",EDGE,"E173.0");Q2=makeQuery(id+"F16.imprint","IMPRINT",FACE,{"disambiguationData":[TD([[makeQuery(id+"F16.imprint","IMPRINT",EDGE,{"derivedFrom":subQ1}),1.0]])]});}
            extrude(context, id + "F17", {"entities" : qUnion([Q0, Q1, Q2]), "oppositeDirection" : true, "depth" : 15 * mm});
        }
        {
            var Q0;
            Q0=makeQuery(id+"F16.imprint","IMPRINT",FACE,{"disambiguationData":[TD([[makeQuery(id+"F16.imprint","IMPRINT",EDGE,{"derivedFrom":sQuery(id+"F16.wireOp",EDGE,"E141")}),1.0]])]});
            var Q1;
            {var subQ3=sQuery(id+"F16.wireOp",EDGE,"E177");Q1=makeQuery(id+"F16.imprint","IMPRINT",FACE,{"disambiguationData":[TD([[makeQuery(id+"F16.imprint","IMPRINT",EDGE,{"derivedFrom":subQ3}),-1.0]])]});}
            var Q2;
            {var subQ4=sQuery(id+"F16.wireOp",EDGE,"E190");Q2=makeQuery(id+"F16.imprint","IMPRINT",FACE,{"disambiguationData":[TD([[makeQuery(id+"F16.imprint","IMPRINT",EDGE,{"derivedFrom":subQ4}),-1.0]])]});}
            extrude(context, id + "F18", {"entities" : qUnion([Q0, Q1, Q2]), "oppositeDirection" : true, "depth" : 390 * mm});
        }
        {
            var Q0;
            Q0=makeQuery(id+"F16.imprint","IMPRINT",FACE,{"disambiguationData":[TD([[makeQuery(id+"F16.imprint","IMPRINT",EDGE,{"derivedFrom":makeQuery(id+"F1.opExtrude","CAP_EDGE",EDGE,{"disambiguationData":[OSD([sQuery(id+"F0.wireOp",EDGE,"E0")])],"isStart":false})}),-1.0]])]});
            cPlane(context, id + "F19", {"entities" : qUnion([Q0]), "cplaneType" : CPlaneType.OFFSET, "offset" : 75 * mm, "oppositeDirection" : true, "width" : 150 * mm, "height" : 150 * mm});
        }
        {
            var Q0;
            Q0=qCreatedBy(id+"F19.planeOp",FACE);
            var sketch = newSketch(context, id + "F20", { "sketchPlane" : qUnion([Q0])});
            skLineSegment(sketch, "E199", {"start": v(541.8, 1086.98) * mm, "end": v(468.16, 1118.23) * mm});
            skLineSegment(sketch, "E200", {"start": v(541.8, 1086.98) * mm, "end": v(510.54, 1013.33) * mm});
            skLineSegment(sketch, "E201", {"start": v(510.54, 1013.33) * mm, "end": v(505.94, 1015.29) * mm});
            skLineSegment(sketch, "E202", {"start": v(503.3, 1021.84) * mm, "end": v(524.78, 1072.47) * mm});
            skLineSegment(sketch, "E203", {"start": v(519.48, 1085.58) * mm, "end": v(468.86, 1107.08) * mm});
            skLineSegment(sketch, "E204", {"start": v(466.2, 1113.63) * mm, "end": v(468.16, 1118.23) * mm});
            skLineSegment(sketch, "E205", {"start": v(2432.53, -1208.61) * mm, "end": v(2139.13, -1208.61) * mm, "construction": true});
            skPoint(sketch, "E206.visualSharp", {"position": v(528.69, 1081.68) * mm});
            skArc(sketch, "E206.filletArc", {"start": v(524.78, 1072.47) * mm, "mid": v(524.85, 1080.13) * mm, "end": v(519.48, 1085.58) * mm});
            skPoint(sketch, "E207.visualSharp", {"position": v(464.25, 1109.03) * mm});
            skArc(sketch, "E207.filletArc", {"start": v(466.2, 1113.63) * mm, "mid": v(466.17, 1109.8) * mm, "end": v(468.86, 1107.08) * mm});
            skPoint(sketch, "E208.visualSharp", {"position": v(501.34, 1017.24) * mm});
            skArc(sketch, "E208.filletArc", {"start": v(503.3, 1021.84) * mm, "mid": v(503.26, 1018.02) * mm, "end": v(505.94, 1015.29) * mm});
            skLineSegment(sketch, "E209", {"start": v(0, 0) * mm, "end": v(-82.56, 0) * mm, "construction": true});
            skLineSegment(sketch, "E210", {"start": v(0, 0) * mm, "end": v(0, 124.95) * mm, "construction": true});
            skLineSegment(sketch, "E211", {"start": v(0, 0) * mm, "end": v(302.9, 0) * mm, "construction": true});
            skLineSegment(sketch, "E212.0", {"start": v(0, 6) * mm, "end": v(302.9, 6) * mm, "construction": true});
            skLineSegment(sketch, "E213", {"start": v(0, 6) * mm, "end": v(-80, 6) * mm, "construction": true});
            skLineSegment(sketch, "E214", {"start": v(-80, 6) * mm, "end": v(1212.93, 3051.95) * mm, "construction": true});
            skLineSegment(sketch, "E215.0", {"start": v(-85.71, 18.13) * mm, "end": v(353.5, 1052.84) * mm});
            skLineSegment(sketch, "E216", {"start": v(-80, 6) * mm, "end": v(-174.08, 45.94) * mm, "construction": true});
            skLineSegment(sketch, "E217.0", {"start": v(-76.1, 15.2) * mm, "end": v(-170.18, 55.14) * mm});
            skLineSegment(sketch, "E218.0", {"start": v(507.2, 1031.05) * mm, "end": v(284.24, 1125.69) * mm, "construction": true});
            skLineSegment(sketch, "E219.0", {"start": v(961.62, 2101.6) * mm, "end": v(738.67, 2196.24) * mm, "construction": true});
            skLineSegment(sketch, "E220.0", {"start": v(1341.8, 2997.25) * mm, "end": v(1118.85, 3091.89) * mm});
            skLineSegment(sketch, "E221.0", {"start": v(52.36, -40.48) * mm, "end": v(72.1, 6) * mm});
            skLineSegment(sketch, "E222.0", {"start": v(522.83, 1067.87) * mm, "end": v(384.75, 1126.48) * mm});
            skLineSegment(sketch, "E223.0", {"start": v(491.57, 994.23) * mm, "end": v(353.5, 1052.84) * mm});
            skLineSegment(sketch, "E224.0", {"start": v(977.25, 2138.42) * mm, "end": v(839.17, 2197.03) * mm});
            skLineSegment(sketch, "E225.0", {"start": v(945.99, 2064.78) * mm, "end": v(807.91, 2123.39) * mm});
            skLineSegment(sketch, "E226.0", {"start": v(-162.85, 41.17) * mm, "end": v(1204.32, 3262.01) * mm});
            skLineSegment(sketch, "E227.trimOffspring", {"start": v(384.75, 1126.48) * mm, "end": v(807.91, 2123.39) * mm});
            skLineSegment(sketch, "E228.trimOffspring", {"start": v(945.99, 2064.78) * mm, "end": v(977.25, 2138.42) * mm});
            skLineSegment(sketch, "E229.trimOffspring", {"start": v(491.57, 994.23) * mm, "end": v(522.83, 1067.87) * mm});
            skLineSegment(sketch, "E230.0", {"start": v(1277.96, 3230.75) * mm, "end": v(1204.32, 3262.01) * mm});
            skLineSegment(sketch, "E231.0", {"start": v(1357.43, 3034.07) * mm, "end": v(1219.35, 3092.68) * mm});
            skLineSegment(sketch, "E232.0", {"start": v(1357.43, 2947.16) * mm, "end": v(1188.1, 3019.04) * mm});
            skLineSegment(sketch, "E233.trimOffspring", {"start": v(839.17, 2197.03) * mm, "end": v(1277.96, 3230.75) * mm});
            skLineSegment(sketch, "E234", {"start": v(1357.43, 3034.07) * mm, "end": v(1357.43, 2947.16) * mm});
            skLineSegment(sketch, "E235", {"start": v(1357.43, 3034.07) * mm, "end": v(1507.43, 3034.07) * mm});
            skLineSegment(sketch, "E236", {"start": v(1357.43, 3034.07) * mm, "end": v(1357.43, 2884.07) * mm});
            skLineSegment(sketch, "E237.0", {"start": v(1383.43, 3024.07) * mm, "end": v(1499.47, 3024.07) * mm});
            skLineSegment(sketch, "E238.0", {"start": v(1367.43, 3008.07) * mm, "end": v(1367.43, 2892.07) * mm});
            skLineSegment(sketch, "E239", {"start": v(1357.43, 2884.07) * mm, "end": v(1359.43, 2884.07) * mm});
            skLineSegment(sketch, "E240", {"start": v(1507.43, 3034.07) * mm, "end": v(1507.47, 3032.25) * mm});
            skArc(sketch, "E241.filletArc", {"start": v(1383.43, 3024.07) * mm, "mid": v(1372.12, 3019.38) * mm, "end": v(1367.43, 3008.07) * mm});
            skPoint(sketch, "E242.visualSharp", {"position": v(1507.65, 3024.07) * mm});
            skArc(sketch, "E242.filletArc", {"start": v(1499.47, 3024.07) * mm, "mid": v(1505.2, 3026.47) * mm, "end": v(1507.47, 3032.25) * mm});
            skPoint(sketch, "E243.visualSharp", {"position": v(1367.43, 2884.07) * mm});
            skArc(sketch, "E243.filletArc", {"start": v(1359.43, 2884.07) * mm, "mid": v(1365.09, 2886.41) * mm, "end": v(1367.43, 2892.07) * mm});
            skLineSegment(sketch, "E244.0", {"start": v(541.8, 1086.98) * mm, "end": v(394.52, 1149.5) * mm, "construction": true});
            skLineSegment(sketch, "E245.0", {"start": v(504.27, 998.55) * mm, "end": v(541.8, 1086.98) * mm, "construction": true});
            skLineSegment(sketch, "E246", {"start": v(996.22, 2157.52) * mm, "end": v(922.58, 2188.78) * mm});
            skLineSegment(sketch, "E247", {"start": v(996.22, 2157.52) * mm, "end": v(964.96, 2083.88) * mm});
            skLineSegment(sketch, "E248", {"start": v(964.96, 2083.88) * mm, "end": v(960.36, 2085.84) * mm});
            skLineSegment(sketch, "E249", {"start": v(957.71, 2092.4) * mm, "end": v(979.2, 2143.02) * mm});
            skLineSegment(sketch, "E250", {"start": v(973.9, 2156.13) * mm, "end": v(923.28, 2177.62) * mm});
            skLineSegment(sketch, "E251", {"start": v(920.63, 2184.18) * mm, "end": v(922.58, 2188.78) * mm});
            skPoint(sketch, "E252.visualSharp", {"position": v(983.1, 2152.22) * mm});
            skArc(sketch, "E252.filletArc", {"start": v(979.2, 2143.02) * mm, "mid": v(979.27, 2150.67) * mm, "end": v(973.9, 2156.13) * mm});
            skArc(sketch, "E253.filletArc", {"start": v(920.63, 2184.18) * mm, "mid": v(920.6, 2180.35) * mm, "end": v(923.28, 2177.62) * mm});
            skPoint(sketch, "E254.visualSharp", {"position": v(955.76, 2087.79) * mm});
            skArc(sketch, "E254.filletArc", {"start": v(957.71, 2092.4) * mm, "mid": v(957.68, 2088.57) * mm, "end": v(960.36, 2085.84) * mm});
            skLineSegment(sketch, "E255.0", {"start": v(958.69, 2069.1) * mm, "end": v(996.22, 2157.52) * mm});
            skLineSegment(sketch, "E256.trimOffspring", {"start": v(858.15, 2216.13) * mm, "end": v(848.94, 2220.04) * mm});
            skLineSegment(sketch, "E257", {"start": v(1219.35, 3092.68) * mm, "end": v(1250.61, 3166.32) * mm});
            skLineSegment(sketch, "E258", {"start": v(1250.61, 3166.32) * mm, "end": v(1324.25, 3135.06) * mm});
            skLineSegment(sketch, "E259", {"start": v(1324.25, 3135.06) * mm, "end": v(1293, 3061.42) * mm});
            skLineSegment(sketch, "E260", {"start": v(1293, 3061.42) * mm, "end": v(1219.35, 3092.68) * mm});
            skCircle(sketch, "E261", {"center": v(1271.8, 3113.87) * mm, "radius": 12.89 * mm});
            skSolve(sketch);
        }
        {
            var Q0;
            {var subQ0=sQuery(id+"F20.wireOp",EDGE,"E230.0");Q0=makeQuery(id+"F20.imprint","IMPRINT",FACE,{"disambiguationData":[TD([[makeQuery(id+"F20.imprint","IMPRINT",EDGE,{"derivedFrom":subQ0}),1.0]])]});}
            var Q1;
            Q1=makeQuery(id+"F20.imprint","IMPRINT",FACE,{"disambiguationData":[TD([[makeQuery(id+"F20.imprint","IMPRINT",EDGE,{"derivedFrom":sQuery(id+"F20.wireOp",EDGE,"E257")}),-1.0]])]});
            var Q2;
            {var subQ5=sQuery(id+"F20.wireOp",EDGE,"E222.0");Q2=makeQuery(id+"F20.imprint","IMPRINT",FACE,{"disambiguationData":[TD([[makeQuery(id+"F20.imprint","IMPRINT",EDGE,{"derivedFrom":subQ5}),1.0]])]});}
            var Q3;
            {var subQ4=sQuery(id+"F20.wireOp",EDGE,"E231.0");Q3=makeQuery(id+"F20.imprint","IMPRINT",FACE,{"disambiguationData":[TD([[makeQuery(id+"F20.imprint","IMPRINT",EDGE,{"derivedFrom":subQ4}),1.0]])]});}
            extrude(context, id + "F21", {"entities" : qUnion([Q0, Q1, Q2, Q3]), "oppositeDirection" : true, "depth" : 15 * mm});
        }
        {
            var Q0;
            Q0=makeQuery(id+"F17.opExtrude","SWEPT_BODY",BODY,{"disambiguationData":[OSD([sQuery(id+"F16.wireOp",EDGE,"E157.0"),sQuery(id+"F16.wireOp",EDGE,"E159.0"),sQuery(id+"F16.wireOp",EDGE,"E164.0"),sQuery(id+"F16.wireOp",EDGE,"E165.0"),sQuery(id+"F16.wireOp",EDGE,"E166.0"),sQuery(id+"F16.wireOp",EDGE,"E167.0"),sQuery(id+"F16.wireOp",EDGE,"E168.0"),sQuery(id+"F16.wireOp",EDGE,"E169.trimOffspring"),sQuery(id+"F16.wireOp",EDGE,"E170.trimOffspring"),sQuery(id+"F16.wireOp",EDGE,"E171.trimOffspring"),sQuery(id+"F16.wireOp",EDGE,"E172.0"),sQuery(id+"F16.wireOp",EDGE,"E173.0"),sQuery(id+"F16.wireOp",EDGE,"E174.0"),sQuery(id+"F16.wireOp",EDGE,"E175.trimOffspring"),sQuery(id+"F16.wireOp",EDGE,"E178"),sQuery(id+"F16.wireOp",EDGE,"E191")])]});
            transform(context, id + "F22", {"entities" : qUnion([Q0]), "transformType" : TransformType.TRANSLATION_3D, "dx" : 0 * mm, "dy" : 150 * mm, "dz" : 0 * mm, "makeCopy" : true});
        }
        {
            var Q0;
            Q0=makeQuery(id+"F22.opPattern","COPY",BODY,{"derivedFrom":makeQuery(id+"F17.opExtrude","SWEPT_BODY",BODY,{"disambiguationData":[OSD([sQuery(id+"F16.wireOp",EDGE,"E157.0"),sQuery(id+"F16.wireOp",EDGE,"E159.0"),sQuery(id+"F16.wireOp",EDGE,"E164.0"),sQuery(id+"F16.wireOp",EDGE,"E165.0"),sQuery(id+"F16.wireOp",EDGE,"E166.0"),sQuery(id+"F16.wireOp",EDGE,"E167.0"),sQuery(id+"F16.wireOp",EDGE,"E168.0"),sQuery(id+"F16.wireOp",EDGE,"E169.trimOffspring"),sQuery(id+"F16.wireOp",EDGE,"E170.trimOffspring"),sQuery(id+"F16.wireOp",EDGE,"E171.trimOffspring"),sQuery(id+"F16.wireOp",EDGE,"E172.0"),sQuery(id+"F16.wireOp",EDGE,"E173.0"),sQuery(id+"F16.wireOp",EDGE,"E174.0"),sQuery(id+"F16.wireOp",EDGE,"E175.trimOffspring"),sQuery(id+"F16.wireOp",EDGE,"E178"),sQuery(id+"F16.wireOp",EDGE,"E191")])]}),"instanceName":"1"});
            transform(context, id + "F23", {"entities" : qUnion([Q0]), "transformType" : TransformType.TRANSLATION_3D, "dx" : 0 * mm, "dy" : 75 * mm, "dz" : 0 * mm, "makeCopy" : false});
        }
        {
            var Q0;
            Q0=makeQuery(id+"F17.opExtrude","SWEPT_BODY",BODY,{"disambiguationData":[OSD([sQuery(id+"F16.wireOp",EDGE,"E157.0"),sQuery(id+"F16.wireOp",EDGE,"E159.0"),sQuery(id+"F16.wireOp",EDGE,"E164.0"),sQuery(id+"F16.wireOp",EDGE,"E165.0"),sQuery(id+"F16.wireOp",EDGE,"E166.0"),sQuery(id+"F16.wireOp",EDGE,"E167.0"),sQuery(id+"F16.wireOp",EDGE,"E168.0"),sQuery(id+"F16.wireOp",EDGE,"E169.trimOffspring"),sQuery(id+"F16.wireOp",EDGE,"E170.trimOffspring"),sQuery(id+"F16.wireOp",EDGE,"E171.trimOffspring"),sQuery(id+"F16.wireOp",EDGE,"E172.0"),sQuery(id+"F16.wireOp",EDGE,"E173.0"),sQuery(id+"F16.wireOp",EDGE,"E174.0"),sQuery(id+"F16.wireOp",EDGE,"E175.trimOffspring"),sQuery(id+"F16.wireOp",EDGE,"E178"),sQuery(id+"F16.wireOp",EDGE,"E191")])]});
            transform(context, id + "F24", {"entities" : qUnion([Q0]), "transformType" : TransformType.TRANSLATION_3D, "dx" : 0 * mm, "dy" : 150 * mm, "dz" : 0 * mm, "makeCopy" : true});
        }
        {
            var Q0;
            Q0=makeQuery(id+"F21.opExtrude","SWEPT_BODY",BODY,{"disambiguationData":[OSD([sQuery(id+"F20.wireOp",EDGE,"E215.0"),sQuery(id+"F20.wireOp",EDGE,"E217.0"),sQuery(id+"F20.wireOp",EDGE,"E222.0"),sQuery(id+"F20.wireOp",EDGE,"E223.0"),sQuery(id+"F20.wireOp",EDGE,"E224.0"),sQuery(id+"F20.wireOp",EDGE,"E225.0"),sQuery(id+"F20.wireOp",EDGE,"E226.0"),sQuery(id+"F20.wireOp",EDGE,"E227.trimOffspring"),sQuery(id+"F20.wireOp",EDGE,"E228.trimOffspring"),sQuery(id+"F20.wireOp",EDGE,"E229.trimOffspring"),sQuery(id+"F20.wireOp",EDGE,"E230.0"),sQuery(id+"F20.wireOp",EDGE,"E231.0"),sQuery(id+"F20.wireOp",EDGE,"E232.0"),sQuery(id+"F20.wireOp",EDGE,"E233.trimOffspring"),sQuery(id+"F20.wireOp",EDGE,"E236"),sQuery(id+"F20.wireOp",EDGE,"E249"),sQuery(id+"F20.wireOp",EDGE,"E258"),sQuery(id+"F20.wireOp",EDGE,"E259"),sQuery(id+"F20.wireOp",EDGE,"E261")])]});
            transform(context, id + "F25", {"entities" : qUnion([Q0]), "transformType" : TransformType.TRANSLATION_3D, "dx" : 0 * mm, "dy" : 225 * mm, "dz" : 0 * mm, "makeCopy" : true});
        }
        {
            var Q0;
            Q0=makeQuery(id+"F22.opPattern","COPY",BODY,{"derivedFrom":makeQuery(id+"F17.opExtrude","SWEPT_BODY",BODY,{"disambiguationData":[OSD([sQuery(id+"F16.wireOp",EDGE,"E157.0"),sQuery(id+"F16.wireOp",EDGE,"E159.0"),sQuery(id+"F16.wireOp",EDGE,"E164.0"),sQuery(id+"F16.wireOp",EDGE,"E165.0"),sQuery(id+"F16.wireOp",EDGE,"E166.0"),sQuery(id+"F16.wireOp",EDGE,"E167.0"),sQuery(id+"F16.wireOp",EDGE,"E168.0"),sQuery(id+"F16.wireOp",EDGE,"E169.trimOffspring"),sQuery(id+"F16.wireOp",EDGE,"E170.trimOffspring"),sQuery(id+"F16.wireOp",EDGE,"E171.trimOffspring"),sQuery(id+"F16.wireOp",EDGE,"E172.0"),sQuery(id+"F16.wireOp",EDGE,"E173.0"),sQuery(id+"F16.wireOp",EDGE,"E174.0"),sQuery(id+"F16.wireOp",EDGE,"E175.trimOffspring"),sQuery(id+"F16.wireOp",EDGE,"E178"),sQuery(id+"F16.wireOp",EDGE,"E191")])]}),"instanceName":"1"});
            transform(context, id + "F26", {"entities" : qUnion([Q0]), "transformType" : TransformType.TRANSLATION_3D, "dx" : 0 * mm, "dy" : 150 * mm, "dz" : 0 * mm, "makeCopy" : true});
        }
    });
